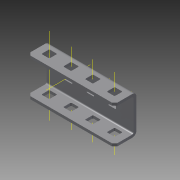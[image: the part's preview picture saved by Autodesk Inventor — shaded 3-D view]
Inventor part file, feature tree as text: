
AUTODESK INVENTOR PART (.ipt)
format: ipt  version: 2015 (Build 190159000, 159)  size: 225,280 bytes
history: native  units: in
note: dims shown in document units (in); Inventor stores cm internally (conversion verified against a paired STEP export)
features: other x16, pattern_linear x2, imported_body x1
ambient origin geometry x8: Origin, YZ Plane, XZ Plane, XY Plane, X Axis, Y Axis, Z Axis, Center Point
bodies: Body1 (feature_tree)
feature tree (19):
  other  "C-Channel Coupler"
  other  "LPattern3"
  other  "back axis"
  other  "front axis"
  other  "top axis"
  pattern_linear  "top axes"  Count1=3 Spacing1=0.5in
  pattern_linear  "Rectangular Pattern2"  Count1=4 Spacing1=0.5in
  imported_body  "Base1"
  other  "Work Point1"
  other  "Work Point2"
  other  "Work Point3"
  other  "Work Axis4"
  other  "Work Axis5"
  other  "Work Axis6"
  other  "Work Axis7"
  other  "Work Axis8"
  other  "Work Axis9"
  other  "Work Axis10"
  other  "Work Axis11"
